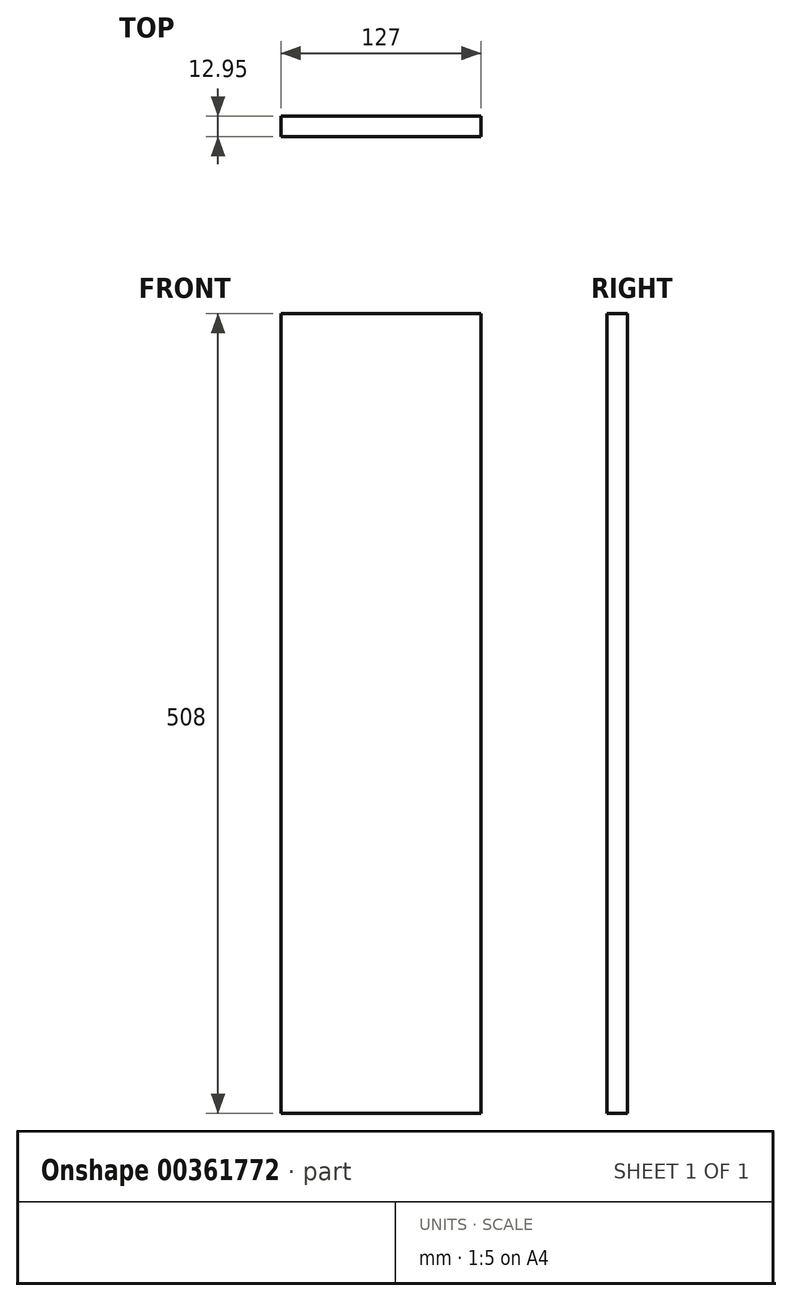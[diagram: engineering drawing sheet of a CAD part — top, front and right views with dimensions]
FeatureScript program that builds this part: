
annotation { "Feature Type Name" : "Feature", "Feature Type Description" : "" }
export const myFeature = defineFeature(function(context is Context, id is Id, definition is map)
    precondition{}
    {
        {
            var Q0;
            Q0=qCreatedBy(makeId("Front.planeOp"),FACE);
            var sketch = newSketch(context, id + "F0", { "sketchPlane" : qUnion([Q0])});
            skLineSegment(sketch, "E0.bottom", {"start": v(-63.5, 254) * mm, "end": v(63.5, 254) * mm});
            skLineSegment(sketch, "E0.top", {"start": v(-63.5, -254) * mm, "end": v(63.5, -254) * mm});
            skLineSegment(sketch, "E0.left", {"start": v(-63.5, 254) * mm, "end": v(-63.5, -254) * mm});
            skLineSegment(sketch, "E0.right", {"start": v(63.5, 254) * mm, "end": v(63.5, -254) * mm});
            skPoint(sketch, "E0.middle", {"position": v(0, 0) * mm});
            skSolve(sketch);
        }
        {
            var Q0;
            Q0 = qSketchRegion(id + "F0", true);
            extrude(context, id + "F1", {"entities" : qUnion([Q0]), "depth" : 12.95 * mm});
        }
    });
